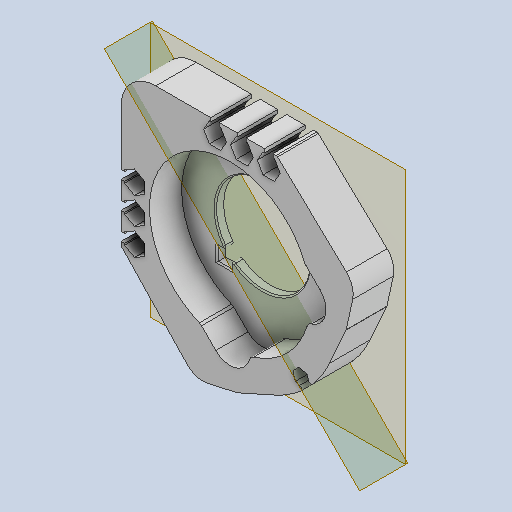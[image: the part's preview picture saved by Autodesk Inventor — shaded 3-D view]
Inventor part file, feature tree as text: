
AUTODESK INVENTOR PART (.ipt)
format: ipt  version: 2022 (Build 260153000, 153)  size: 763,392 bytes
history: native  units: in
note: dims shown in document units (in); Inventor stores cm internally (conversion verified against a paired STEP export)
features: reference x8, extrude x3, fillet x3, sketch x3, other x3, plane x2, chamfer x1, projected_geometry x1
ambient origin geometry x8: Origin, YZ Plane, XZ Plane, XY Plane, X Axis, Y Axis, Z Axis, Center Point
bodies: Solid1 (feature_tree)
feature tree (24):
  plane  "Work Plane1"
  extrude  "Extrusion1"  Depth=1.0in
  extrude  "Extrusion2"  Depth=0.1575in
  plane  "Work Plane2"
  fillet  "Fillet3"  Radius=0.7874in
  fillet  "Fillet4"  Radius=0.1575in
  chamfer  "Chamfer3"  Distance=1.0in
  extrude  "Extrusion3"  TaperAngle=315.0deg  [1 undecoded]
  fillet  "Fillet2"  Radius=0.75in
  sketch  "Sketch1"  dims[d0=1.75in d1=1.0in]
  reference  "Reference1"
  sketch  "Sketch2"  dims[d2=45.0deg d3=0.1679in d4=0.7874in d6=360.0deg d8=0.1575in d9=0.0in]
  projected_geometry  "Projected Loop1"
  sketch  "Sketch3"  dims[d10=1.0in d11=1.0in d12=315.0deg d13=0.75in d14=135.0deg d15=0.6in d16=0.0in d18=45.0deg d19=0.0in d20=0.0in d21=0.125in d23=3.0in d24=0.261in d25=0.0394in d26=0.125in d33=0.0236in d34=0.125in d35=45.0deg]
  reference  "Reference2"
  reference  "Reference3"
  reference  "Reference4"
  reference  "Reference5"
  reference  "Reference6"
  reference  "Reference7"
  reference  "Reference8"
  other  "<userpath>\Documents\CAD\guardSwerve1\Assembly1.iam"
  other  "Assembly1.iam"
  other  "midblock"
note: 1 required parameter value undecoded (feature->parameter linkage not recoverable at this tier; creation-order binding heuristic only, values carry confidence <= 0.55)
